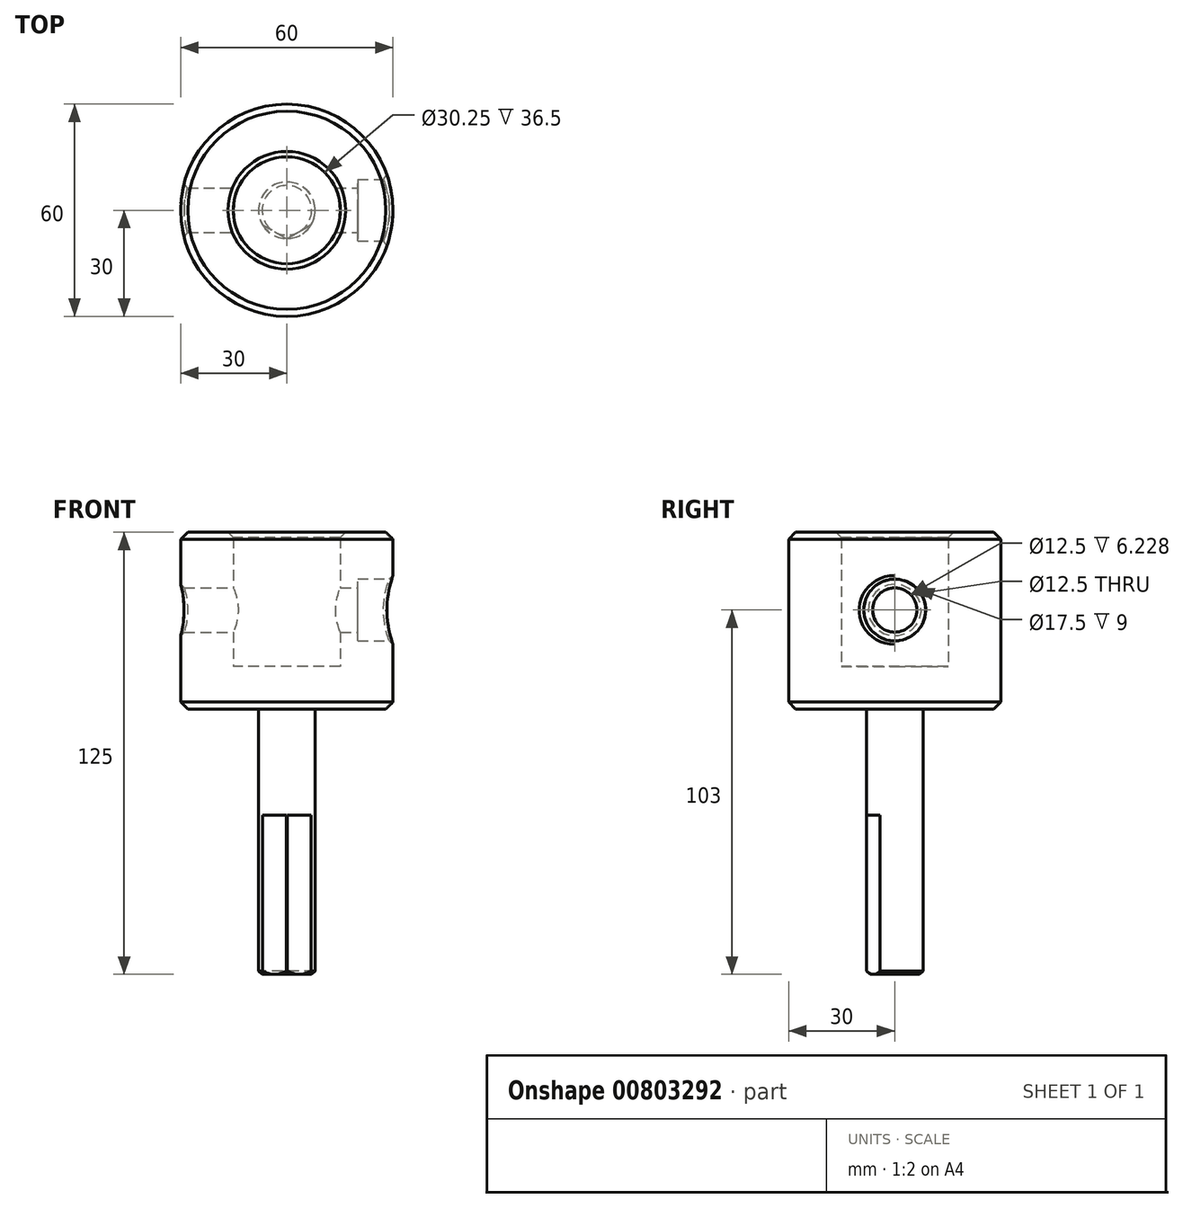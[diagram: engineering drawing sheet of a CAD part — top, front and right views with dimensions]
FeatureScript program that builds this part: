
annotation { "Feature Type Name" : "Feature", "Feature Type Description" : "" }
export const myFeature = defineFeature(function(context is Context, id is Id, definition is map)
    precondition{}
    {
        {
            var Q0;
            Q0=qCreatedBy(makeId("Top.planeOp"),FACE);
            var sketch = newSketch(context, id + "F0", { "sketchPlane" : qUnion([Q0])});
            skCircle(sketch, "E0", {"center": v(0, 0) * mm, "radius": 30 * mm});
            skCircle(sketch, "E1", {"center": v(0, 0) * mm, "radius": 15.12 * mm});
            skCircle(sketch, "E2", {"center": v(0, 0) * mm, "radius": 8 * mm});
            skSolve(sketch);
        }
        {
            var Q0;
            Q0=makeQuery(id+"F0.imprint","IMPRINT",FACE,{"disambiguationData":[TD([[makeQuery(id+"F0.imprint","IMPRINT",EDGE,{"derivedFrom":sQuery(id+"F0.wireOp",EDGE,"E0")}),1.0]])]});
            extrude(context, id + "F1", {"entities" : qUnion([Q0]), "depth" : 125 * mm, "offsetDistance" : 25 * mm, "hasSecondDirection" : true, "secondDirectionOppositeDirection" : false, "secondDirectionDepth" : 75 * mm});
        }
        {
            var Q0;
            Q0=makeQuery(id+"F0.imprint","IMPRINT",FACE,{"disambiguationData":[TD([[makeQuery(id+"F0.imprint","IMPRINT",EDGE,{"derivedFrom":sQuery(id+"F0.wireOp",EDGE,"E1")}),1.0]])]});
            var Q1;
            Q1=makeQuery(id+"F0.imprint","IMPRINT",FACE,{"disambiguationData":[TD([[makeQuery(id+"F0.imprint","IMPRINT",EDGE,{"derivedFrom":sQuery(id+"F0.wireOp",EDGE,"E2")}),1.0]])]});
            extrude(context, id + "F2", {"entities" : qUnion([Q0, Q1]), "operationType" : NewBodyOperationType.ADD, "depth" : 87 * mm, "offsetDistance" : 25 * mm, "hasSecondDirection" : true, "secondDirectionOppositeDirection" : false, "secondDirectionDepth" : 75 * mm});
        }
        {
            var Q0;
            Q0=makeQuery(id+"F0.imprint","IMPRINT",FACE,{"disambiguationData":[TD([[makeQuery(id+"F0.imprint","IMPRINT",EDGE,{"derivedFrom":sQuery(id+"F0.wireOp",EDGE,"E2")}),1.0]])]});
            extrude(context, id + "F3", {"entities" : qUnion([Q0]), "operationType" : NewBodyOperationType.ADD, "depth" : 75 * mm, "offsetDistance" : 25 * mm});
        }
        {
            var Q0;
            Q0=qCreatedBy(makeId("Right.planeOp"),FACE);
            cPlane(context, id + "F4", {"entities" : qUnion([Q0]), "cplaneType" : CPlaneType.OFFSET, "offset" : 30 * mm, "width" : 150 * mm, "height" : 150 * mm});
        }
        {
            var Q0;
            Q0=qCreatedBy(id+"F4.planeOp",FACE);
            var sketch = newSketch(context, id + "F5", { "sketchPlane" : qUnion([Q0])});
            skCircle(sketch, "E3", {"center": v(0, 103) * mm, "radius": 6.25 * mm});
            skCircle(sketch, "E4", {"center": v(0, 103) * mm, "radius": 8.75 * mm});
            skSolve(sketch);
        }
        {
            var Q0;
            Q0=makeQuery(id+"F5.imprint","IMPRINT",FACE,{"disambiguationData":[TD([[makeQuery(id+"F5.imprint","IMPRINT",EDGE,{"derivedFrom":sQuery(id+"F5.wireOp",EDGE,"E3")}),1.0]])]});
            extrude(context, id + "F6", {"entities" : qUnion([Q0]), "operationType" : NewBodyOperationType.REMOVE, "oppositeDirection" : true, "depth" : 66.2 * mm, "offsetDistance" : 25 * mm});
        }
        {
            var Q0;
            Q0=makeQuery(id+"F5.imprint","IMPRINT",FACE,{"disambiguationData":[TD([[makeQuery(id+"F5.imprint","IMPRINT",EDGE,{"derivedFrom":sQuery(id+"F5.wireOp",EDGE,"E3")}),-1.0]])]});
            extrude(context, id + "F7", {"entities" : qUnion([Q0]), "operationType" : NewBodyOperationType.REMOVE, "oppositeDirection" : true, "depth" : 10 * mm, "offsetDistance" : 25 * mm});
        }
        {
            var Q0;
            Q0=qCreatedBy(makeId("Top.planeOp"),FACE);
            var sketch = newSketch(context, id + "F8", { "sketchPlane" : qUnion([Q0])});
            skCircle(sketch, "E5", {"center": v(0, 0) * mm, "radius": 10 * mm});
            skCircle(sketch, "E6.cCircle", {"center": v(0, 0) * mm, "radius": 7 * mm, "construction": true});
            skLineSegment(sketch, "E6.0", {"start": v(7, -4.04) * mm, "end": v(0, -8.08) * mm});
            skLineSegment(sketch, "E6.1", {"start": v(0, -8.08) * mm, "end": v(-7, -4.04) * mm});
            skLineSegment(sketch, "E6.2", {"start": v(-7, -4.04) * mm, "end": v(-7, 4.04) * mm});
            skLineSegment(sketch, "E6.3", {"start": v(-7, 4.04) * mm, "end": v(0, 8.08) * mm});
            skLineSegment(sketch, "E6.4", {"start": v(0, 8.08) * mm, "end": v(7, 4.04) * mm});
            skLineSegment(sketch, "E6.5", {"start": v(7, 4.04) * mm, "end": v(7, -4.04) * mm});
            skPoint(sketch, "E6.0.midPoint", {"position": v(3.5, -6.06) * mm});
            skLineSegment(sketch, "E7", {"start": v(0, -16.18) * mm, "end": v(0, 16.01) * mm, "construction": true});
            skLineSegment(sketch, "E8", {"start": v(-7, -8.13) * mm, "end": v(-7, 9.13) * mm});
            skLineSegment(sketch, "E9", {"start": v(7, -7.75) * mm, "end": v(7, 9) * mm});
            skSolve(sketch);
        }
        {
            var Q0;
            {var subQ0=sQuery(id+"F8.wireOp",EDGE,"E8");var subQ1=sQuery(id+"F8.wireOp",EDGE,"E5");var subQ2=makeQuery(id+"F8.imprint","INTERSECT",VERTEX,{"disambiguationData":[OD(0.0)],"derivedFrom":[subQ1,subQ0]});Q0=makeQuery(id+"F8.imprint","IMPRINT",FACE,{"disambiguationData":[TD([[makeQuery(id+"F8.imprint","IMPRINT",EDGE,{"disambiguationData":[TD([[subQ2,-1.0]])],"derivedFrom":subQ1}),1.0]])]});}
            var Q1;
            {var subQ0=sQuery(id+"F8.wireOp",EDGE,"E9");var subQ1=sQuery(id+"F8.wireOp",EDGE,"E5");var subQ2=makeQuery(id+"F8.imprint","INTERSECT",VERTEX,{"disambiguationData":[OD(0.0)],"derivedFrom":[subQ1,subQ0]});Q1=makeQuery(id+"F8.imprint","IMPRINT",FACE,{"disambiguationData":[TD([[makeQuery(id+"F8.imprint","IMPRINT",EDGE,{"disambiguationData":[TD([[subQ2,1.0]])],"derivedFrom":subQ1}),1.0]])]});}
            extrude(context, id + "F9", {"entities" : qUnion([Q0, Q1]), "operationType" : NewBodyOperationType.REMOVE, "depth" : 45 * mm, "offsetDistance" : 25 * mm});
        }
        {
            var Q0;
            Q0=makeQuery(id+"F1.opExtrude","CAP_EDGE",EDGE,{"disambiguationData":[OSD([sQuery(id+"F0.wireOp",EDGE,"E0")])],"isStart":false});
            var Q1;
            Q1=makeQuery(id+"F1.opExtrude","CAP_EDGE",EDGE,{"disambiguationData":[OSD([sQuery(id+"F0.wireOp",EDGE,"E0")])],"isStart":true});
            chamfer(context, id + "F10", {"entities" : qUnion([Q0, Q1]), "width" : 2 * mm, "tangentPropagation" : true});
        }
        {
            var Q0;
            Q0=makeQuery(id+"F1.opExtrude","CAP_EDGE",EDGE,{"disambiguationData":[OSD([sQuery(id+"F0.wireOp",EDGE,"E1")])],"isStart":false});
            chamfer(context, id + "F11", {"entities" : qUnion([Q0]), "width" : 1.5 * mm, "tangentPropagation" : true});
        }
        {
            var Q0;
            Q0=makeQuery(id+"F6.boolean.opBoolean","INTERSECT",EDGE,{"disambiguationData":[OD(0.0)],"derivedFrom":[makeQuery(id+"F1.opExtrude","SWEPT_FACE",FACE,{"disambiguationData":[OSD([sQuery(id+"F0.wireOp",EDGE,"E0")])]}),makeQuery(id+"F6.opExtrude","SWEPT_FACE",FACE,{"disambiguationData":[OSD([sQuery(id+"F5.wireOp",EDGE,"E3")])]})]});
            var Q1;
            Q1=makeQuery(id+"F7.boolean.opBoolean","INTERSECT",EDGE,{"derivedFrom":[makeQuery(id+"F1.opExtrude","SWEPT_FACE",FACE,{"disambiguationData":[OSD([sQuery(id+"F0.wireOp",EDGE,"E0")])]}),makeQuery(id+"F7.opExtrude","SWEPT_FACE",FACE,{"disambiguationData":[OSD([sQuery(id+"F5.wireOp",EDGE,"E4")])]})]});
            var Q2;
            Q2=makeQuery(id+"F9.boolean.opBoolean","SPLIT",EDGE,{"disambiguationData":[OD(0.0)],"derivedFrom":makeQuery(id+"F3.opExtrude","CAP_EDGE",EDGE,{"disambiguationData":[OSD([sQuery(id+"F0.wireOp",EDGE,"E2")])],"isStart":true})});
            var Q3;
            Q3=makeQuery(id+"F9.boolean.opBoolean","SPLIT",EDGE,{"disambiguationData":[OD(1.0)],"derivedFrom":makeQuery(id+"F3.opExtrude","CAP_EDGE",EDGE,{"disambiguationData":[OSD([sQuery(id+"F0.wireOp",EDGE,"E2")])],"isStart":true})});
            chamfer(context, id + "F12", {"entities" : qUnion([Q0, Q1, Q2, Q3]), "width" : 1 * mm, "tangentPropagation" : true});
        }
    });
